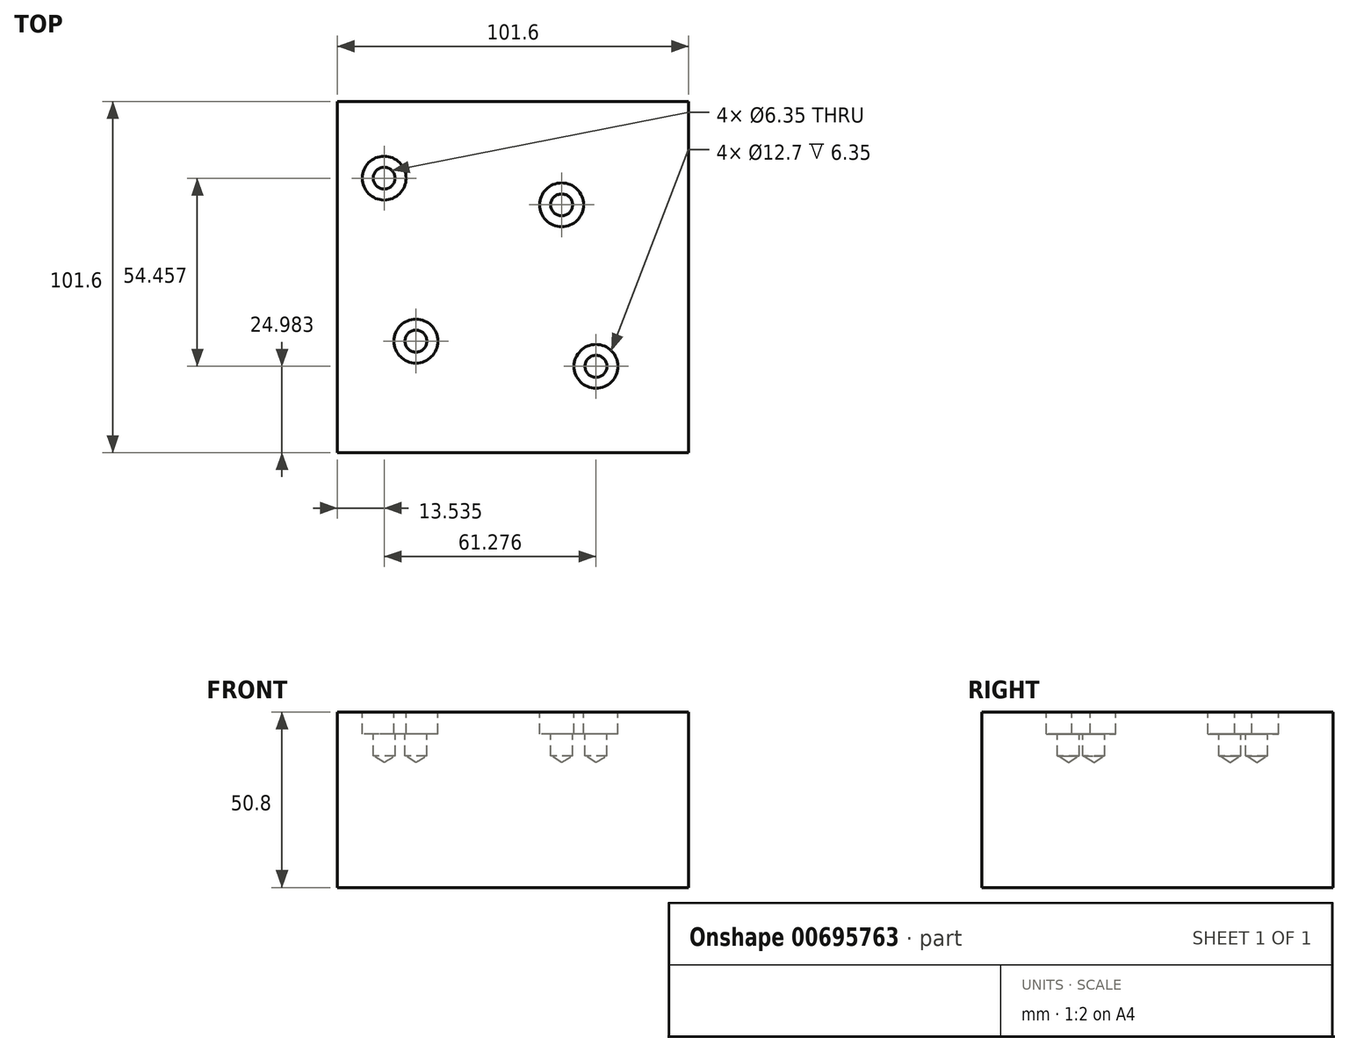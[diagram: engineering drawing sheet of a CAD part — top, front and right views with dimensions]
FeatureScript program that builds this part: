
annotation { "Feature Type Name" : "Feature", "Feature Type Description" : "" }
export const myFeature = defineFeature(function(context is Context, id is Id, definition is map)
    precondition{}
    {
        {
            var Q0;
            Q0=qCreatedBy(makeId("Front.planeOp"),FACE);
            var sketch = newSketch(context, id + "F0", { "sketchPlane" : qUnion([Q0])});
            skLineSegment(sketch, "E0.bottom", {"start": v(-50.9, -0.84) * mm, "end": v(50.7, -0.84) * mm});
            skLineSegment(sketch, "E0.top", {"start": v(-50.9, -51.64) * mm, "end": v(50.7, -51.64) * mm});
            skLineSegment(sketch, "E0.left", {"start": v(-50.9, -0.84) * mm, "end": v(-50.9, -51.64) * mm});
            skLineSegment(sketch, "E0.right", {"start": v(50.7, -0.84) * mm, "end": v(50.7, -51.64) * mm});
            skSolve(sketch);
        }
        {
            var Q0;
            Q0=makeQuery(id+"F0.imprint","IMPRINT",FACE,{"disambiguationData":[TD([[makeQuery(id+"F0.imprint","IMPRINT",EDGE,{"derivedFrom":sQuery(id+"F0.wireOp",EDGE,"E0.bottom")}),-1.0]])]});
            extrude(context, id + "F1", {"entities" : qUnion([Q0]), "endBound" : BoundingType.SYMMETRIC, "depth" : 101.6 * mm, "offsetDistance" : 25.4 * mm});
        }
        {
            var Q0;
            Q0=makeQuery(id+"F1.opExtrude","SWEPT_FACE",FACE,{"disambiguationData":[OSD([sQuery(id+"F0.wireOp",EDGE,"E0.bottom")])]});
            var sketch = newSketch(context, id + "F2", { "sketchPlane" : qUnion([Q0])});
            skPoint(sketch, "E1", {"position": v(-37.35, 28.64) * mm});
            skPoint(sketch, "E2", {"position": v(14, 20.9) * mm});
            skPoint(sketch, "E3", {"position": v(23.92, -25.82) * mm});
            skPoint(sketch, "E4", {"position": v(-28.16, -18.51) * mm});
            skSolve(sketch);
        }
        {
            var Q0;
            Q0=sQuery(id+"F2.wireOp",VERTEX,"E1");
            var Q1;
            Q1=sQuery(id+"F2.wireOp",VERTEX,"E2");
            var Q2;
            Q2=sQuery(id+"F2.wireOp",VERTEX,"E3");
            var Q3;
            Q3=sQuery(id+"F2.wireOp",VERTEX,"E4");
            var Q4;
            Q4=makeQuery(id+"F1.opExtrude","SWEPT_BODY",BODY,{"disambiguationData":[OSD([sQuery(id+"F0.wireOp",EDGE,"E0.bottom"),sQuery(id+"F0.wireOp",EDGE,"E0.top"),sQuery(id+"F0.wireOp",EDGE,"E0.left"),sQuery(id+"F0.wireOp",EDGE,"E0.right")])]});
            hole(context, id + "F3", {"style" : HoleStyle.C_BORE, "endStyle" : HoleEndStyle.BLIND, "holeDiameter" : 6.35 * mm, "cBoreDiameter" : 12.7 * mm, "cBoreDepth" : 6.35 * mm, "majorDiameter" : 6.35 * mm, "holeDepth" : 12.7 * mm, "isTappedThrough" : true, "tappedDepth" : 12.7 * mm, "tapClearance" : 3, "locations" : qUnion([Q0, Q1, Q2, Q3]), "scope" : qUnion([Q4])});
        }
    });
